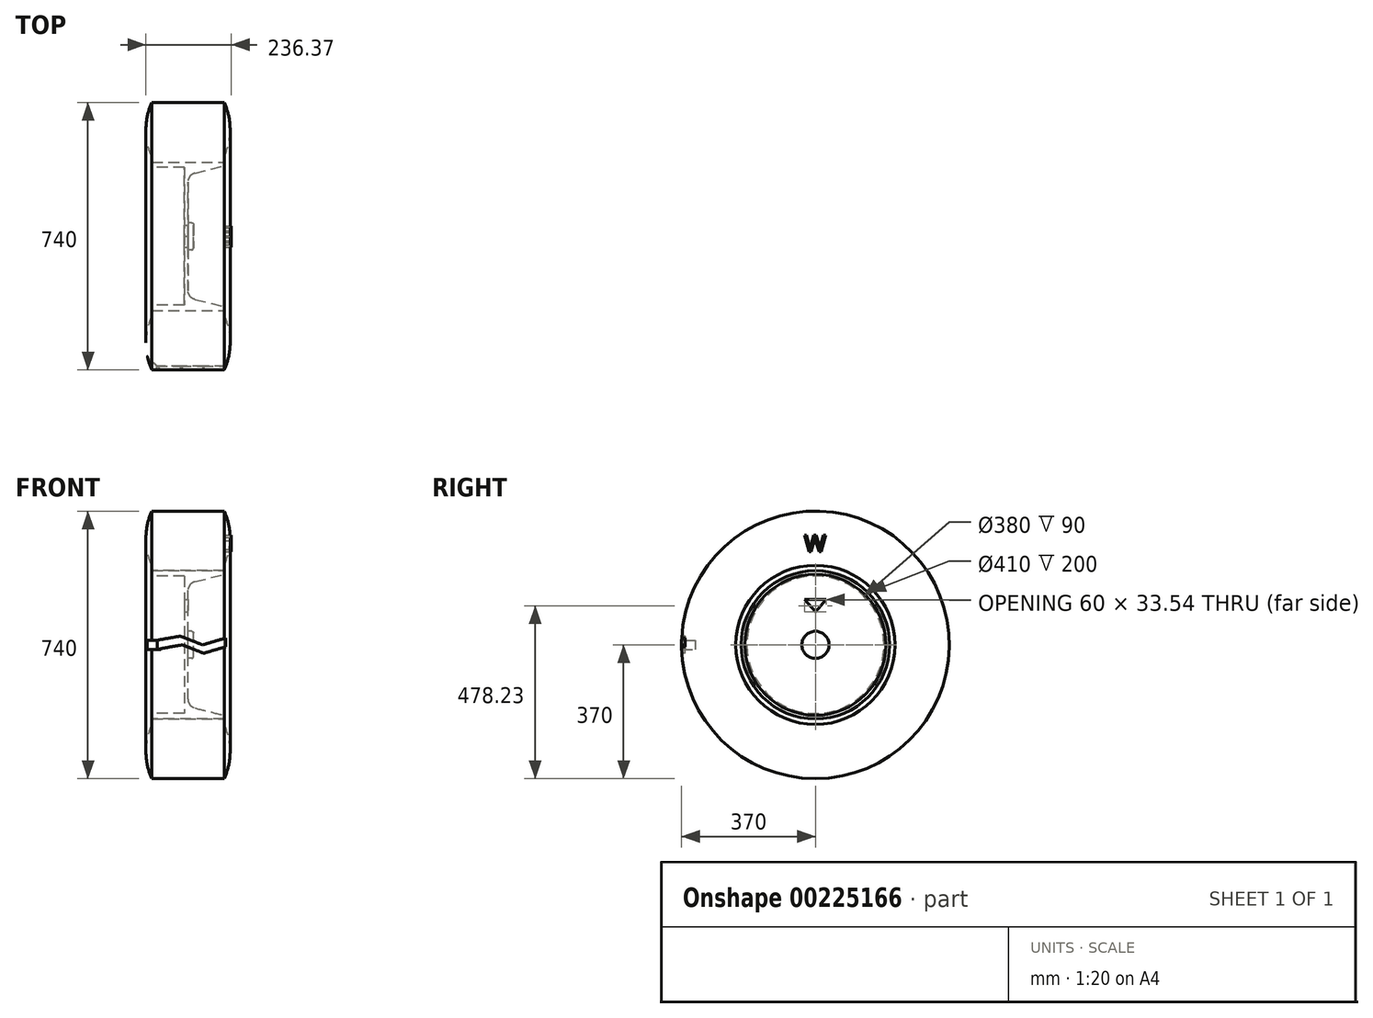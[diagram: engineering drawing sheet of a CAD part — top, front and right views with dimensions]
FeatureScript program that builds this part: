
annotation { "Feature Type Name" : "Feature", "Feature Type Description" : "" }
export const myFeature = defineFeature(function(context is Context, id is Id, definition is map)
    precondition{}
    {
        {
            var Q0;
            Q0=qCreatedBy(makeId("Front.planeOp"),FACE);
            var sketch = newSketch(context, id + "F0", { "sketchPlane" : qUnion([Q0])});
            skLineSegment(sketch, "E0", {"start": v(0, 0) * mm, "end": v(100, 0) * mm});
            skLineSegment(sketch, "E1", {"start": v(100, 0) * mm, "end": v(100, 220) * mm});
            skArc(sketch, "E2", {"start": v(100, 220) * mm, "mid": v(116.37, 295) * mm, "end": v(100, 370) * mm});
            skLineSegment(sketch, "E3", {"start": v(0, 4.06) * mm, "end": v(0, 97.72) * mm, "construction": true});
            skLineSegment(sketch, "E4", {"start": v(100, 370) * mm, "end": v(0, 370) * mm});
            skLineSegment(sketch, "E5.MirrorCS", {"start": v(0, 0) * mm, "end": v(-100, 0) * mm});
            skLineSegment(sketch, "E6.MirrorCS", {"start": v(-100, 0) * mm, "end": v(-100, 220) * mm});
            skArc(sketch, "E7.MirrorCS", {"start": v(-100, 220) * mm, "mid": v(-116.37, 295) * mm, "end": v(-100, 370) * mm});
            skLineSegment(sketch, "E8.MirrorCS", {"start": v(-100, 370) * mm, "end": v(0, 370) * mm});
            skSolve(sketch);
        }
        {
            var Q0;
            Q0=makeQuery(id+"F0.imprint","IMPRINT",FACE,{"disambiguationData":[TD([[makeQuery(id+"F0.imprint","IMPRINT",EDGE,{"derivedFrom":sQuery(id+"F0.wireOp",EDGE,"E0")}),1.0]])]});
            var Q1;
            Q1=sQuery(id+"F0.wireOp",EDGE,"E5.MirrorCS");
            revolve(context, id + "F1", {"entities" : qUnion([Q0]), "axis" : qUnion([Q1]), "revolveType" : RevolveType.FULL});
        }
        {
            var Q0;
            Q0=qCreatedBy(makeId("Top.planeOp"),FACE);
            var sketch = newSketch(context, id + "F2", { "sketchPlane" : qUnion([Q0])});
            skLineSegment(sketch, "E9", {"start": v(-70, -375) * mm, "end": v(-120, -325) * mm});
            skLineSegment(sketch, "E10", {"start": v(-120, -325) * mm, "end": v(-120, -375) * mm});
            skLineSegment(sketch, "E11", {"start": v(-120, -375) * mm, "end": v(-70, -375) * mm});
            skSolve(sketch);
        }
        {
            var Q0;
            Q0 = qSketchRegion(id + "F2", true);
            extrude(context, id + "F3", {"entities" : qUnion([Q0]), "operationType" : NewBodyOperationType.REMOVE, "oppositeDirection" : true, "depth" : 25 * mm, "symmetric" : true});
        }
        {
            var Q0;
            Q0=makeQuery(id+"F1.opRevolve","SWEPT_FACE",FACE,{"disambiguationData":[OSD([sQuery(id+"F0.wireOp",EDGE,"E6.MirrorCS")])]});
            var sketch = newSketch(context, id + "F4", { "sketchPlane" : qUnion([Q0])});
            skCircle(sketch, "E12", {"center": v(0, 0) * mm, "radius": 205 * mm});
            skSolve(sketch);
        }
        {
            var Q0;
            Q0 = qSketchRegion(id + "F4", true);
            extrude(context, id + "F5", {"entities" : qUnion([Q0]), "operationType" : NewBodyOperationType.REMOVE, "endBound" : BoundingType.THROUGH_ALL, "oppositeDirection" : true, "depth" : 15 * mm});
        }
        {
            var Q0;
            Q0=makeQuery(id+"F3.boolean.opBoolean","INTERSECT",VERTEX,{"derivedFrom":[makeQuery(id+"F1.opRevolve","SWEPT_FACE",FACE,{"disambiguationData":[OSD([sQuery(id+"F0.wireOp",EDGE,"E4"),sQuery(id+"F0.wireOp",EDGE,"E8.MirrorCS")])]}),makeQuery(id+"F1.opRevolve","SWEPT_FACE",FACE,{"disambiguationData":[OSD([sQuery(id+"F0.wireOp",EDGE,"E7.MirrorCS")])]}),makeQuery(id+"F3.opExtrude","CAP_FACE",FACE,{"disambiguationData":[OSD([sQuery(id+"F2.wireOp",EDGE,"E9"),sQuery(id+"F2.wireOp",EDGE,"E10"),sQuery(id+"F2.wireOp",EDGE,"E11")])],"isStart":true})]});
            var Q1;
            {var subQ0=sQuery(id+"F2.wireOp",EDGE,"E9");Q1=makeQuery(id+"F3.boolean.opBoolean","INTERSECT",VERTEX,{"derivedFrom":[makeQuery(id+"F1.opRevolve","SWEPT_FACE",FACE,{"disambiguationData":[OSD([sQuery(id+"F0.wireOp",EDGE,"E4"),sQuery(id+"F0.wireOp",EDGE,"E8.MirrorCS")])]}),makeQuery(id+"F3.opExtrude","SWEPT_FACE",FACE,{"disambiguationData":[OSD([subQ0])]}),makeQuery(id+"F3.opExtrude","CAP_FACE",FACE,{"disambiguationData":[OSD([subQ0,sQuery(id+"F2.wireOp",EDGE,"E10"),sQuery(id+"F2.wireOp",EDGE,"E11")])],"isStart":true})]});}
            var Q2;
            Q2=makeQuery(id+"F3.boolean.opBoolean","INTERSECT",VERTEX,{"derivedFrom":[makeQuery(id+"F1.opRevolve","SWEPT_FACE",FACE,{"disambiguationData":[OSD([sQuery(id+"F0.wireOp",EDGE,"E4"),sQuery(id+"F0.wireOp",EDGE,"E8.MirrorCS")])]}),makeQuery(id+"F1.opRevolve","SWEPT_FACE",FACE,{"disambiguationData":[OSD([sQuery(id+"F0.wireOp",EDGE,"E7.MirrorCS")])]}),makeQuery(id+"F3.opExtrude","CAP_FACE",FACE,{"disambiguationData":[OSD([sQuery(id+"F2.wireOp",EDGE,"E9"),sQuery(id+"F2.wireOp",EDGE,"E10"),sQuery(id+"F2.wireOp",EDGE,"E11")])],"isStart":false})]});
            cPlane(context, id + "F6", {"entities" : qUnion([Q0, Q1, Q2]), "cplaneType" : CPlaneType.THREE_POINT, "offset" : 25 * mm, "width" : 150 * mm, "height" : 150 * mm});
        }
        {
            var Q0;
            Q0=qCreatedBy(id+"F6.planeOp",FACE);
            var sketch = newSketch(context, id + "F7", { "sketchPlane" : qUnion([Q0])});
            skLineSegment(sketch, "E13", {"start": v(-87.6, 12.5) * mm, "end": v(-21.04, 24.08) * mm});
            skLineSegment(sketch, "E14", {"start": v(-21.04, 24.08) * mm, "end": v(40.19, 0) * mm});
            skLineSegment(sketch, "E15", {"start": v(40.19, 0) * mm, "end": v(122.4, 24.08) * mm});
            skLineSegment(sketch, "E16", {"start": v(122.4, 24.08) * mm, "end": v(122.4, 0) * mm});
            skLineSegment(sketch, "E17", {"start": v(122.4, 0) * mm, "end": v(43.22, -23.2) * mm});
            skLineSegment(sketch, "E18", {"start": v(43.22, -23.2) * mm, "end": v(-15.74, 0) * mm});
            skLineSegment(sketch, "E19", {"start": v(-15.74, 0) * mm, "end": v(-87.6, -12.5) * mm});
            skLineSegment(sketch, "E20", {"start": v(-87.6, -12.5) * mm, "end": v(-87.6, 12.5) * mm});
            skSolve(sketch);
        }
        {
            var Q0;
            Q0 = qSketchRegion(id + "F7", true);
            extrude(context, id + "F8", {"entities" : qUnion([Q0]), "operationType" : NewBodyOperationType.REMOVE, "oppositeDirection" : true, "depth" : 10 * mm, "hasSecondDirection" : true, "secondDirectionOppositeDirection" : false, "secondDirectionDepth" : 25 * mm});
        }
        {
            var Q0;
            Q0 = qSketchRegion(id + "F4", true);
            extrude(context, id + "F9", {"entities" : qUnion([Q0]), "operationType" : NewBodyOperationType.REMOVE, "endBound" : BoundingType.THROUGH_ALL, "oppositeDirection" : true, "depth" : 25 * mm});
        }
        {
            var Q0;
            Q0=qCreatedBy(makeId("Front.planeOp"),FACE);
            var sketch = newSketch(context, id + "F10", { "sketchPlane" : qUnion([Q0])});
            skLineSegment(sketch, "E21", {"start": v(100, 205) * mm, "end": v(100, 195) * mm});
            skLineSegment(sketch, "E22", {"start": v(100, 195) * mm, "end": v(18.94, 174.73) * mm});
            skLineSegment(sketch, "E23", {"start": v(0, 150.48) * mm, "end": v(0, 0) * mm});
            skLineSegment(sketch, "E24", {"start": v(0, 0) * mm, "end": v(-100, 0) * mm});
            skLineSegment(sketch, "E25", {"start": v(100, 205) * mm, "end": v(-100, 205) * mm});
            skLineSegment(sketch, "E26", {"start": v(-100, 0) * mm, "end": v(-100, 205) * mm});
            skPoint(sketch, "E27.visualSharp", {"position": v(0, 170) * mm});
            skArc(sketch, "E27.filletArc", {"start": v(18.94, 174.73) * mm, "mid": v(5.3, 165.87) * mm, "end": v(0, 150.48) * mm});
            skLineSegment(sketch, "E28", {"start": v(0, 0) * mm, "end": v(-177.76, 0) * mm, "construction": true});
            skSolve(sketch);
        }
        {
            var Q0;
            Q0 = qSketchRegion(id + "F10", true);
            var Q1;
            Q1=sQuery(id+"F10.wireOp",EDGE,"E28");
            revolve(context, id + "F11", {"entities" : qUnion([Q0]), "axis" : qUnion([Q1]), "revolveType" : RevolveType.FULL});
        }
        {
            var Q0;
            Q0=makeQuery(id+"F11.opRevolve","SWEPT_FACE",FACE,{"disambiguationData":[OSD([sQuery(id+"F10.wireOp",EDGE,"E23")])]});
            var sketch = newSketch(context, id + "F12", { "sketchPlane" : qUnion([Q0])});
            skLineSegment(sketch, "E29", {"start": v(0, 125) * mm, "end": v(-30, 125) * mm});
            skLineSegment(sketch, "E30", {"start": v(-30, 125) * mm, "end": v(0, 91.46) * mm});
            skLineSegment(sketch, "E31", {"start": v(0, 91.46) * mm, "end": v(30, 125) * mm});
            skLineSegment(sketch, "E32", {"start": v(0, 125) * mm, "end": v(30, 125) * mm});
            skSolve(sketch);
        }
        {
            var Q0;
            Q0 = qSketchRegion(id + "F12", true);
            extrude(context, id + "F13", {"entities" : qUnion([Q0]), "operationType" : NewBodyOperationType.REMOVE, "endBound" : BoundingType.THROUGH_ALL, "oppositeDirection" : true, "depth" : 25 * mm});
        }
        {
            var Q0;
            Q0=makeQuery(id+"F11.opRevolve","SWEPT_FACE",FACE,{"disambiguationData":[OSD([sQuery(id+"F10.wireOp",EDGE,"E23")])]});
            var sketch = newSketch(context, id + "F14", { "sketchPlane" : qUnion([Q0])});
            skCircle(sketch, "E33", {"center": v(0, 0) * mm, "radius": 37.5 * mm});
            skSolve(sketch);
        }
        {
            var Q0;
            Q0 = qSketchRegion(id + "F14", true);
            extrude(context, id + "F15", {"entities" : qUnion([Q0]), "depth" : 15 * mm});
        }
        {
            var Q0;
            Q0=makeQuery(id+"F15.opExtrude","CAP_EDGE",EDGE,{"disambiguationData":[OSD([sQuery(id+"F14.wireOp",EDGE,"E33")])],"isStart":false});
            fillet(context, id + "F16", {"entities" : qUnion([Q0]), "radius" : 5 * mm, "tangentPropagation" : true, "allowEdgeOverflow" : false});
        }
        {
            var Q0;
            Q0=makeQuery(id+"F4.imprint","IMPRINT",FACE,{"disambiguationData":[TD([[makeQuery(id+"F4.imprint","IMPRINT",EDGE,{"derivedFrom":sQuery(id+"F4.wireOp",EDGE,"E12")}),1.0]])]});
            var sketch = newSketch(context, id + "F17", { "sketchPlane" : qUnion([Q0])});
            skCircle(sketch, "E34", {"center": v(0, 0) * mm, "radius": 190 * mm});
            skSolve(sketch);
        }
        {
            var Q0;
            Q0 = qSketchRegion(id + "F17", true);
            extrude(context, id + "F18", {"entities" : qUnion([Q0]), "operationType" : NewBodyOperationType.REMOVE, "oppositeDirection" : true, "depth" : 90 * mm});
        }
        {
            var Q0;
            Q0=qCreatedBy(makeId("Right.planeOp"),FACE);
            cPlane(context, id + "F19", {"entities" : qUnion([Q0]), "cplaneType" : CPlaneType.OFFSET, "offset" : 120 * mm, "width" : 150 * mm, "height" : 150 * mm});
        }
        {
            var Q0;
            Q0=qCreatedBy(id+"F19.planeOp",FACE);
            var sketch = newSketch(context, id + "F20", { "sketchPlane" : qUnion([Q0])});
            skCircle(sketch, "E35", {"center": v(0, 0) * mm, "radius": 258.95 * mm, "construction": true});
            skText(sketch, "E36", { "text": "W", "fontName": "OpenSans-Regular.ttf"});
            const initialGuessF20  = {"E36": [-0.031, 0.25709, 1, 0, 0.04668]};
            skSetInitialGuess(sketch, initialGuessF20);
            skSolve(sketch);
        }
        {
            var Q0;
            Q0 = qSketchRegion(id + "F20", true);
            extrude(context, id + "F21", {"entities" : qUnion([Q0]), "oppositeDirection" : true, "depth" : 20 * mm});
        }
    });
